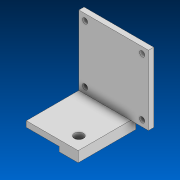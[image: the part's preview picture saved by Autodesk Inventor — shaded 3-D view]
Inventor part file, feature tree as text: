
AUTODESK INVENTOR PART (.ipt)
format: ipt  version: 2022 (Build 260153000, 153)  size: 123,904 bytes
history: native  units: in
note: dims shown in document units (in); Inventor stores cm internally (conversion verified against a paired STEP export)
features: sketch x3, extrude x2, hole x2
ambient origin geometry x8: Origin, YZ Plane, XZ Plane, XY Plane, X Axis, Y Axis, Z Axis, Center Point
bodies: Solid1 (feature_tree)
feature tree (7):
  sketch  "Sketch1"  dims[d1=2.65in d2=2.65in]
  extrude  "Extrusion1"  Depth=2.65in
  hole  "Hole1"  [1 undecoded]
  extrude  "Extrusion2"  Depth=0.675in
  hole  "Hole2"  [1 undecoded]
  sketch  "Sketch2"  dims[d3=2.175in d4=0.2in d5=0.0in]
  sketch  "Sketch3"  dims[d6=0.2in d7=0.75in d8=0.375in d9=0.25in d10=0.5635in d11=1.0in d12=0.8108in d14=0.675in d16=0.4in d17=0.18in d18=1.25in d19=2.2in d20=0.0in d21=0.25in d22=0.5in d23=0.18in d24=0.75in d25=0.35in d26=0.2in d27=0.5635in d28=1.0in d29=0.8108in]
note: 2 required parameter values undecoded (feature->parameter linkage not recoverable at this tier; creation-order binding heuristic only, values carry confidence <= 0.55)
